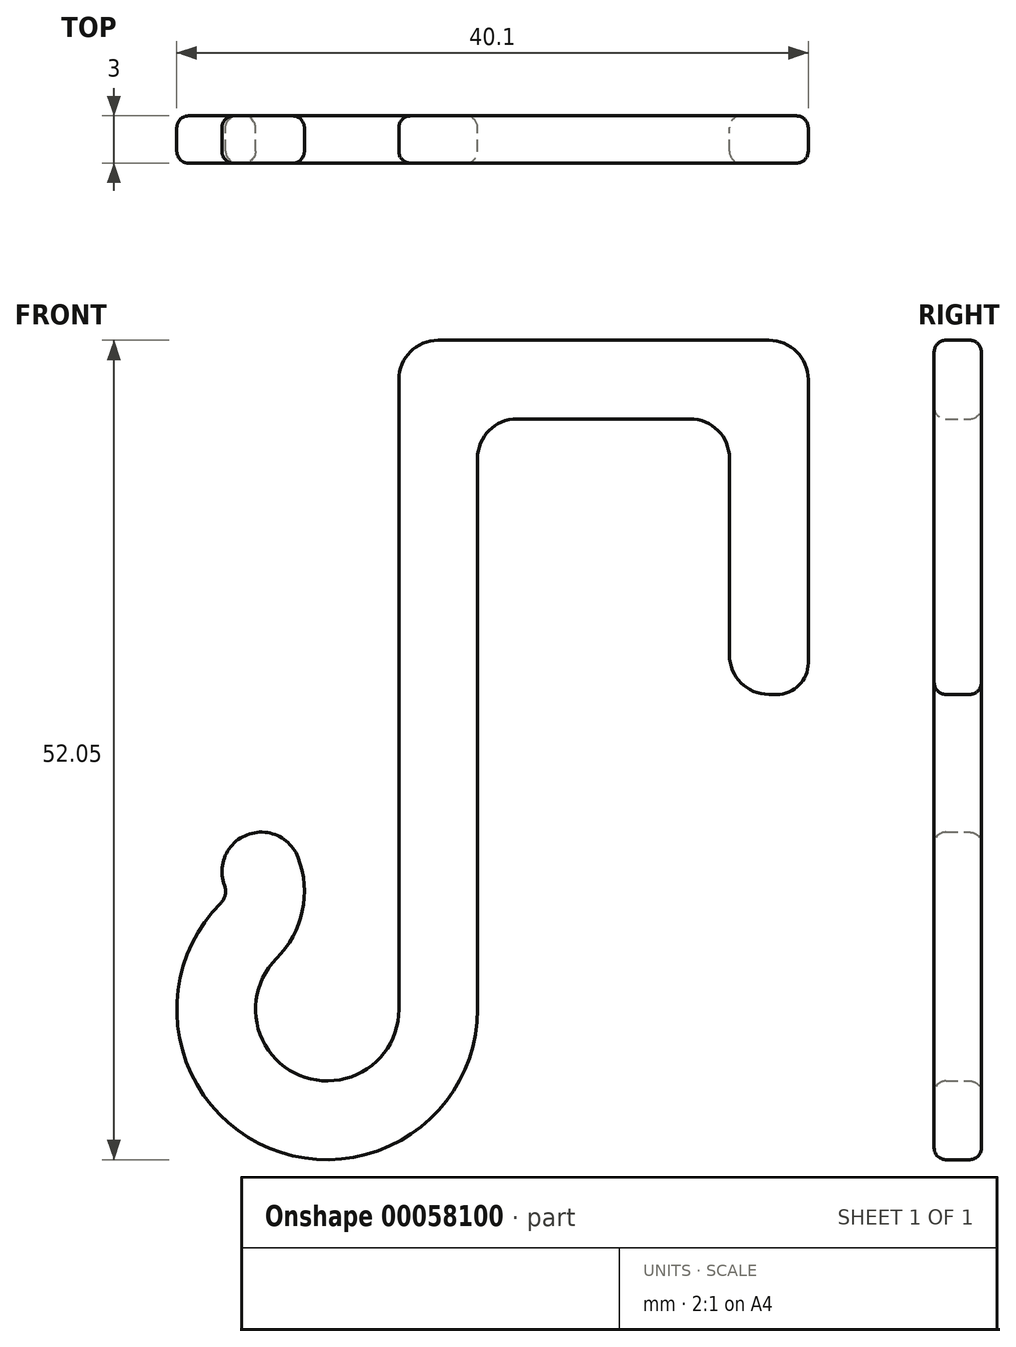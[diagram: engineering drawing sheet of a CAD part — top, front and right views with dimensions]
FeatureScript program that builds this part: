
annotation { "Feature Type Name" : "Feature", "Feature Type Description" : "" }
export const myFeature = defineFeature(function(context is Context, id is Id, definition is map)
    precondition{}
    {
        {
            var Q0;
            Q0=qCreatedBy(makeId("Front.planeOp"),FACE);
            var sketch = newSketch(context, id + "F0", { "sketchPlane" : qUnion([Q0])});
            skLineSegment(sketch, "E0", {"start": v(0, 20) * mm, "end": v(0, -20) * mm});
            skLineSegment(sketch, "E1", {"start": v(0, 20) * mm, "end": v(21, 20) * mm});
            skLineSegment(sketch, "E2", {"start": v(21, 20) * mm, "end": v(21, -1) * mm});
            skPoint(sketch, "E3", {"position": v(-12.04, -15.01) * mm});
            skArc(sketch, "E4", {"start": v(-12.04, -15.01) * mm, "mid": v(-9.75, -26.51) * mm, "end": v(0, -20) * mm});
            skPoint(sketch, "E5", {"position": v(-12.04, -10.02) * mm});
            skArc(sketch, "E6", {"start": v(-12.04, -15.01) * mm, "mid": v(-11, -12.52) * mm, "end": v(-12.04, -10.02) * mm});
            skPoint(sketch, "E7", {"position": v(-7.05, -27.05) * mm});
            skLineSegment(sketch, "E8", {"start": v(-12.04, -15.01) * mm, "end": v(-7.05, -20) * mm});
            skLineSegment(sketch, "E9", {"start": v(-7.05, -20) * mm, "end": v(-7.05, -27.05) * mm});
            skLineSegment(sketch, "E10.0", {"start": v(18.5, 15) * mm, "end": v(18.5, 2.5) * mm});
            skArc(sketch, "E10.1", {"start": v(-13.8, -13.25) * mm, "mid": v(-13.52, -12.73) * mm, "end": v(-13.57, -12.14) * mm});
            skArc(sketch, "E10.2", {"start": v(-13.8, -13.25) * mm, "mid": v(-10.7, -28.82) * mm, "end": v(2.5, -20) * mm});
            skLineSegment(sketch, "E10.3", {"start": v(2.5, 15) * mm, "end": v(2.5, -20) * mm});
            skLineSegment(sketch, "E10.4", {"start": v(5, 17.5) * mm, "end": v(16, 17.5) * mm});
            skLineSegment(sketch, "E11.0", {"start": v(23.5, 20) * mm, "end": v(23.5, 2) * mm});
            skArc(sketch, "E11.1", {"start": v(-10.27, -16.78) * mm, "mid": v(-8.63, -13.77) * mm, "end": v(-8.9, -10.35) * mm});
            skArc(sketch, "E11.2", {"start": v(-10.27, -16.78) * mm, "mid": v(-8.8, -24.2) * mm, "end": v(-2.5, -20) * mm});
            skLineSegment(sketch, "E11.3", {"start": v(-2.5, 20) * mm, "end": v(-2.5, -20) * mm});
            skLineSegment(sketch, "E11.4", {"start": v(0, 22.5) * mm, "end": v(21, 22.5) * mm});
            skLineSegment(sketch, "E12", {"start": v(-13.04, -9.52) * mm, "end": v(-13.04, -9.52) * mm});
            skLineSegment(sketch, "E13", {"start": v(21, 0) * mm, "end": v(21.5, 0) * mm});
            skPoint(sketch, "E14.visualSharp", {"position": v(-2.5, 22.5) * mm});
            skArc(sketch, "E14.filletArc", {"start": v(0, 22.5) * mm, "mid": v(-1.77, 21.77) * mm, "end": v(-2.5, 20) * mm});
            skPoint(sketch, "E15.visualSharp", {"position": v(23.5, 22.5) * mm});
            skArc(sketch, "E15.filletArc", {"start": v(23.5, 20) * mm, "mid": v(22.77, 21.77) * mm, "end": v(21, 22.5) * mm});
            skPoint(sketch, "E16.visualSharp", {"position": v(18.5, 17.5) * mm});
            skArc(sketch, "E16.filletArc", {"start": v(18.5, 15) * mm, "mid": v(17.77, 16.77) * mm, "end": v(16, 17.5) * mm});
            skPoint(sketch, "E17.visualSharp", {"position": v(2.5, 17.5) * mm});
            skArc(sketch, "E17.filletArc", {"start": v(5, 17.5) * mm, "mid": v(3.23, 16.77) * mm, "end": v(2.5, 15) * mm});
            skPoint(sketch, "E18.visualSharp", {"position": v(18.5, 0) * mm});
            skArc(sketch, "E18.filletArc", {"start": v(18.5, 2.5) * mm, "mid": v(19.23, 0.73) * mm, "end": v(21, 0) * mm});
            skPoint(sketch, "E19.visualSharp", {"position": v(23.5, 0) * mm});
            skArc(sketch, "E19.filletArc", {"start": v(21.5, 0) * mm, "mid": v(22.91, 0.59) * mm, "end": v(23.5, 2) * mm});
            skPoint(sketch, "E20.visualSharp", {"position": v(-11.13, -7.53) * mm});
            skArc(sketch, "E20.filletArc", {"start": v(-8.9, -10.35) * mm, "mid": v(-10.74, -8.8) * mm, "end": v(-13.04, -9.52) * mm});
            skPoint(sketch, "E21.visualSharp", {"position": v(-15.07, -11.63) * mm});
            skArc(sketch, "E21.filletArc", {"start": v(-13.04, -9.52) * mm, "mid": v(-13.69, -10.75) * mm, "end": v(-13.57, -12.14) * mm});
            skSolve(sketch);
        }
        {
            var Q0;
            {var subQ6=sQuery(id+"F0.wireOp",EDGE,"E0");Q0=makeQuery(id+"F0.imprint","IMPRINT",FACE,{"disambiguationData":[TD([[makeQuery(id+"F0.imprint","IMPRINT",EDGE,{"derivedFrom":subQ6}),1.0]])]});}
            var Q1;
            {var subQ4=sQuery(id+"F0.wireOp",EDGE,"E0");Q1=makeQuery(id+"F0.imprint","IMPRINT",FACE,{"disambiguationData":[TD([[makeQuery(id+"F0.imprint","IMPRINT",EDGE,{"derivedFrom":subQ4}),-1.0]])]});}
            var Q2;
            {var subQ1=sQuery(id+"F0.wireOp",EDGE,"E4");var subQ3=sQuery(id+"F0.wireOp",EDGE,"E9");var subQ4=makeQuery(id+"F0.imprint","INTERSECT",VERTEX,{"derivedFrom":[subQ1,subQ3]});Q2=makeQuery(id+"F0.imprint","IMPRINT",FACE,{"disambiguationData":[TD([[makeQuery(id+"F0.imprint","IMPRINT",EDGE,{"disambiguationData":[TD([[subQ4,1.0]])],"derivedFrom":subQ3}),-1.0]])]});}
            var Q3;
            {var subQ5=sQuery(id+"F0.wireOp",EDGE,"E11.1");Q3=makeQuery(id+"F0.imprint","IMPRINT",FACE,{"disambiguationData":[TD([[makeQuery(id+"F0.imprint","IMPRINT",EDGE,{"derivedFrom":subQ5}),1.0]])]});}
            extrude(context, id + "F1", {"entities" : qUnion([Q0, Q1, Q2, Q3]), "depth" : 3 * mm});
        }
        {
            var Q0;
            Q0=makeQuery(id+"F1.opExtrude","CAP_FACE",FACE,{"disambiguationData":[OSD([sQuery(id+"F0.wireOp",EDGE,"E10.0"),sQuery(id+"F0.wireOp",EDGE,"E10.1"),sQuery(id+"F0.wireOp",EDGE,"E10.2"),sQuery(id+"F0.wireOp",EDGE,"E10.3"),sQuery(id+"F0.wireOp",EDGE,"E10.4"),sQuery(id+"F0.wireOp",EDGE,"E11.0"),sQuery(id+"F0.wireOp",EDGE,"E11.1"),sQuery(id+"F0.wireOp",EDGE,"E11.2"),sQuery(id+"F0.wireOp",EDGE,"E11.3"),sQuery(id+"F0.wireOp",EDGE,"E11.4"),sQuery(id+"F0.wireOp",EDGE,"E14.filletArc"),sQuery(id+"F0.wireOp",EDGE,"E15.filletArc"),sQuery(id+"F0.wireOp",EDGE,"E16.filletArc"),sQuery(id+"F0.wireOp",EDGE,"E17.filletArc"),sQuery(id+"F0.wireOp",EDGE,"E18.filletArc"),sQuery(id+"F0.wireOp",EDGE,"E19.filletArc"),sQuery(id+"F0.wireOp",EDGE,"E20.filletArc"),sQuery(id+"F0.wireOp",EDGE,"E21.filletArc")])],"isStart":false});
            var Q1;
            Q1=makeQuery(id+"F1.opExtrude","CAP_FACE",FACE,{"disambiguationData":[OSD([sQuery(id+"F0.wireOp",EDGE,"E10.0"),sQuery(id+"F0.wireOp",EDGE,"E10.1"),sQuery(id+"F0.wireOp",EDGE,"E10.2"),sQuery(id+"F0.wireOp",EDGE,"E10.3"),sQuery(id+"F0.wireOp",EDGE,"E10.4"),sQuery(id+"F0.wireOp",EDGE,"E11.0"),sQuery(id+"F0.wireOp",EDGE,"E11.1"),sQuery(id+"F0.wireOp",EDGE,"E11.2"),sQuery(id+"F0.wireOp",EDGE,"E11.3"),sQuery(id+"F0.wireOp",EDGE,"E11.4"),sQuery(id+"F0.wireOp",EDGE,"E14.filletArc"),sQuery(id+"F0.wireOp",EDGE,"E15.filletArc"),sQuery(id+"F0.wireOp",EDGE,"E16.filletArc"),sQuery(id+"F0.wireOp",EDGE,"E17.filletArc"),sQuery(id+"F0.wireOp",EDGE,"E18.filletArc"),sQuery(id+"F0.wireOp",EDGE,"E19.filletArc"),sQuery(id+"F0.wireOp",EDGE,"E20.filletArc"),sQuery(id+"F0.wireOp",EDGE,"E21.filletArc")])],"isStart":true});
            fillet(context, id + "F2", {"entities" : qUnion([Q0, Q1]), "radius" : .75 * mm, "tangentPropagation" : true, "allowEdgeOverflow" : false});
        }
    });
